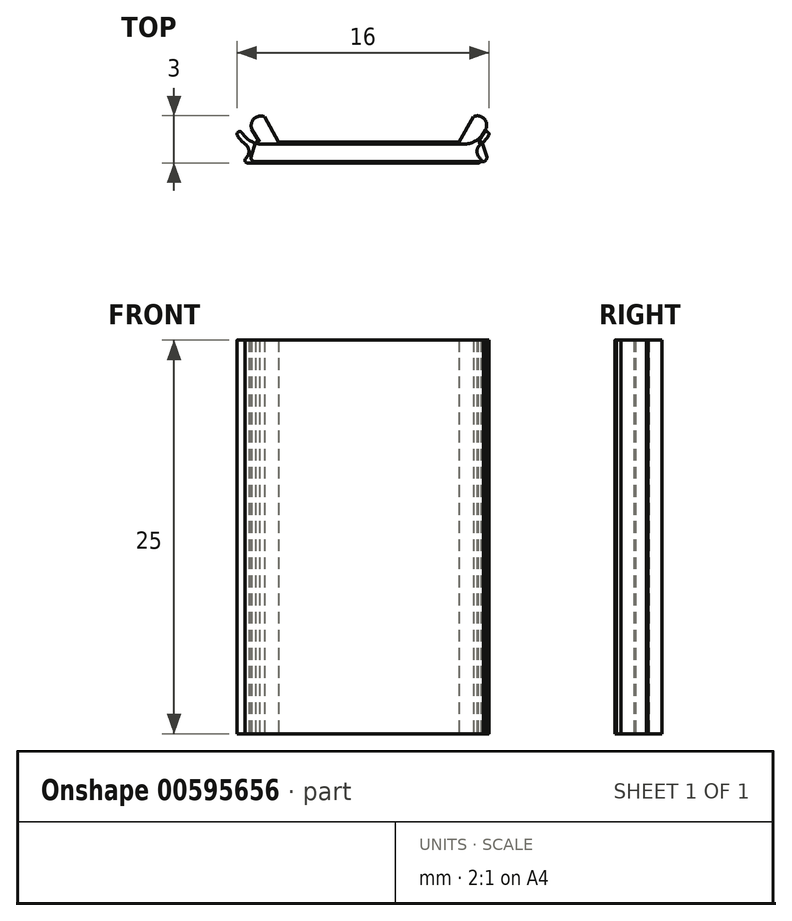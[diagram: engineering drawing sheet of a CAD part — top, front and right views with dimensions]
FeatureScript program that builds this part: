
annotation { "Feature Type Name" : "Feature", "Feature Type Description" : "" }
export const myFeature = defineFeature(function(context is Context, id is Id, definition is map)
    precondition{}
    {
        {
            var Q0;
            Q0=qCreatedBy(makeId("Top.planeOp"),FACE);
            var sketch = newSketch(context, id + "F0", { "sketchPlane" : qUnion([Q0])});
            skLineSegment(sketch, "E0", {"start": v(-62.67, 17.41) * mm, "end": v(-53.63, 1.2) * mm});
            skLineSegment(sketch, "E1", {"start": v(-53.63, 1.2) * mm, "end": v(61.12, 1.2) * mm});
            skLineSegment(sketch, "E2", {"start": v(61.12, 1.2) * mm, "end": v(70.16, 17.41) * mm});
            skArc(sketch, "E3", {"start": v(70.16, 17.41) * mm, "mid": v(77.1, 16.01) * mm, "end": v(77.7, 8.96) * mm});
            skLineSegment(sketch, "E4", {"start": v(77.7, 8.96) * mm, "end": v(73.17, 1.2) * mm});
            skLineSegment(sketch, "E5", {"start": v(73.17, 1.2) * mm, "end": v(75.67, 1.2) * mm});
            skLineSegment(sketch, "E6", {"start": v(75.67, 1.2) * mm, "end": v(78.64, -8.2) * mm});
            skArc(sketch, "E7", {"start": v(78.64, -8.2) * mm, "mid": v(78.1, -10.12) * mm, "end": v(76.38, -11.17) * mm});
            skLineSegment(sketch, "E8", {"start": v(76.38, -11.17) * mm, "end": v(-68.18, -11.17) * mm});
            skArc(sketch, "E9", {"start": v(-68.18, -11.17) * mm, "mid": v(-70.37, -10.39) * mm, "end": v(-71.15, -8.2) * mm});
            skLineSegment(sketch, "E10", {"start": v(-71.15, -8.2) * mm, "end": v(-68.18, 1.2) * mm});
            skLineSegment(sketch, "E11", {"start": v(-68.18, 1.2) * mm, "end": v(-65.68, 1.2) * mm});
            skLineSegment(sketch, "E12", {"start": v(-65.68, 1.2) * mm, "end": v(-70.68, 9.7) * mm});
            skArc(sketch, "E13", {"start": v(-70.68, 9.7) * mm, "mid": v(-69.14, 16.12) * mm, "end": v(-62.67, 17.41) * mm});
            skLineSegment(sketch, "E14", {"start": v(78.64, -11.17) * mm, "end": v(78.64, 17.98) * mm, "construction": true});
            skLineSegment(sketch, "E15", {"start": v(78.64, 17.98) * mm, "end": v(-71.15, 17.98) * mm, "construction": true});
            skLineSegment(sketch, "E16", {"start": v(-71.15, 17.98) * mm, "end": v(-71.15, -11.17) * mm, "construction": true});
            skLineSegment(sketch, "E17", {"start": v(-71.15, -11.17) * mm, "end": v(78.64, -11.17) * mm, "construction": true});
            skSolve(sketch);
        }
        {
            var Q0;
            Q0=makeQuery(id+"F0.imprint","IMPRINT",FACE,{"disambiguationData":[TD([[makeQuery(id+"F0.imprint","IMPRINT",EDGE,{"derivedFrom":sQuery(id+"F0.wireOp",EDGE,"E0")}),-1.0]])]});
            extrude(context, id + "F1", {"entities" : qUnion([Q0]), "depth" : 250 * mm, "offsetDistance" : 25 * mm});
        }
        {
            var Q0;
            Q0=makeQuery(id+"F1.opExtrude","SWEPT_BODY",BODY,{"disambiguationData":[OSD([sQuery(id+"F0.wireOp",EDGE,"E0"),sQuery(id+"F0.wireOp",EDGE,"E1"),sQuery(id+"F0.wireOp",EDGE,"E2"),sQuery(id+"F0.wireOp",EDGE,"E3"),sQuery(id+"F0.wireOp",EDGE,"E4"),sQuery(id+"F0.wireOp",EDGE,"E5"),sQuery(id+"F0.wireOp",EDGE,"E6"),sQuery(id+"F0.wireOp",EDGE,"E7"),sQuery(id+"F0.wireOp",EDGE,"E8"),sQuery(id+"F0.wireOp",EDGE,"E9"),sQuery(id+"F0.wireOp",EDGE,"E10"),sQuery(id+"F0.wireOp",EDGE,"E11"),sQuery(id+"F0.wireOp",EDGE,"E12"),sQuery(id+"F0.wireOp",EDGE,"E13")])]});
            var Q1;
            Q1=qCreatedBy(makeId("Origin.pointOp"),VERTEX);
            transform(context, id + "F2", {"entities" : qUnion([Q0]), "transformType" : TransformType.SCALE_UNIFORMLY, "scale" : 0.1, "scalePoint" : qUnion([Q1]), "makeCopy" : false});
        }
        {
            var Q0;
            Q0=qCreatedBy(makeId("Top.planeOp"),FACE);
            var sketch = newSketch(context, id + "F3", { "sketchPlane" : qUnion([Q0])});
            skArc(sketch, "E18", {"start": v(7.68, 0.72) * mm, "mid": v(7.92, 0.77) * mm, "end": v(7.97, 0.53) * mm});
            skArc(sketch, "E19", {"start": v(7.44, -0.9) * mm, "mid": v(7.49, -1.09) * mm, "end": v(7.33, -1.2) * mm});
            skLineSegment(sketch, "E20", {"start": v(7.32, -1.2) * mm, "end": v(0, -1.2) * mm});
            skLineSegment(sketch, "E21", {"start": v(8, 1.8) * mm, "end": v(0, 1.8) * mm, "construction": true});
            skArc(sketch, "E22", {"start": v(7.48, 0) * mm, "mid": v(7.75, 0.24) * mm, "end": v(7.97, 0.53) * mm});
            skArc(sketch, "E23", {"start": v(6.4, 0) * mm, "mid": v(7.13, 0.2) * mm, "end": v(7.68, 0.72) * mm});
            skLineSegment(sketch, "E24", {"start": v(0, 0) * mm, "end": v(6.4, 0) * mm});
            skLineSegment(sketch, "E25", {"start": v(8, -1.09) * mm, "end": v(8, 1.8) * mm, "construction": true});
            skLineSegment(sketch, "E26", {"start": v(7.5, -4.24) * mm, "end": v(7.5, -1.03) * mm, "construction": true});
            skLineSegment(sketch, "E27", {"start": v(8, 0.8) * mm, "end": v(7.82, 0.8) * mm, "construction": true});
            skArc(sketch, "E28", {"start": v(7.48, 0) * mm, "mid": v(7.24, -0.44) * mm, "end": v(7.44, -0.9) * mm});
            skLineSegment(sketch, "E29", {"start": v(0, 4.56) * mm, "end": v(0, 0) * mm, "construction": true});
            skLineSegment(sketch, "E30.MirrorCS", {"start": v(-7.33, -1.2) * mm, "end": v(0, -1.2) * mm});
            skArc(sketch, "E31.MirrorCS", {"start": v(-7.48, 0) * mm, "mid": v(-7.75, 0.24) * mm, "end": v(-7.97, 0.53) * mm});
            skArc(sketch, "E32.MirrorCS", {"start": v(-7.68, 0.72) * mm, "mid": v(-7.92, 0.77) * mm, "end": v(-7.97, 0.53) * mm});
            skArc(sketch, "E33.MirrorCS", {"start": v(-7.44, -0.9) * mm, "mid": v(-7.49, -1.09) * mm, "end": v(-7.33, -1.2) * mm});
            skArc(sketch, "E34.MirrorCS", {"start": v(-6.4, 0) * mm, "mid": v(-7.13, 0.2) * mm, "end": v(-7.68, 0.72) * mm});
            skLineSegment(sketch, "E35.MirrorCS", {"start": v(-7.5, -4.24) * mm, "end": v(-7.5, -1.03) * mm, "construction": true});
            skArc(sketch, "E36.MirrorCS", {"start": v(-7.48, 0) * mm, "mid": v(-7.24, -0.44) * mm, "end": v(-7.44, -0.9) * mm});
            skLineSegment(sketch, "E37.MirrorCS", {"start": v(0, 0) * mm, "end": v(-6.4, 0) * mm});
            skSolve(sketch);
        }
        {
            var Q0;
            Q0 = qSketchRegion(id + "F3", true);
            extrude(context, id + "F4", {"entities" : qUnion([Q0]), "depth" : 25 * mm, "offsetDistance" : 25 * mm});
        }
    });
